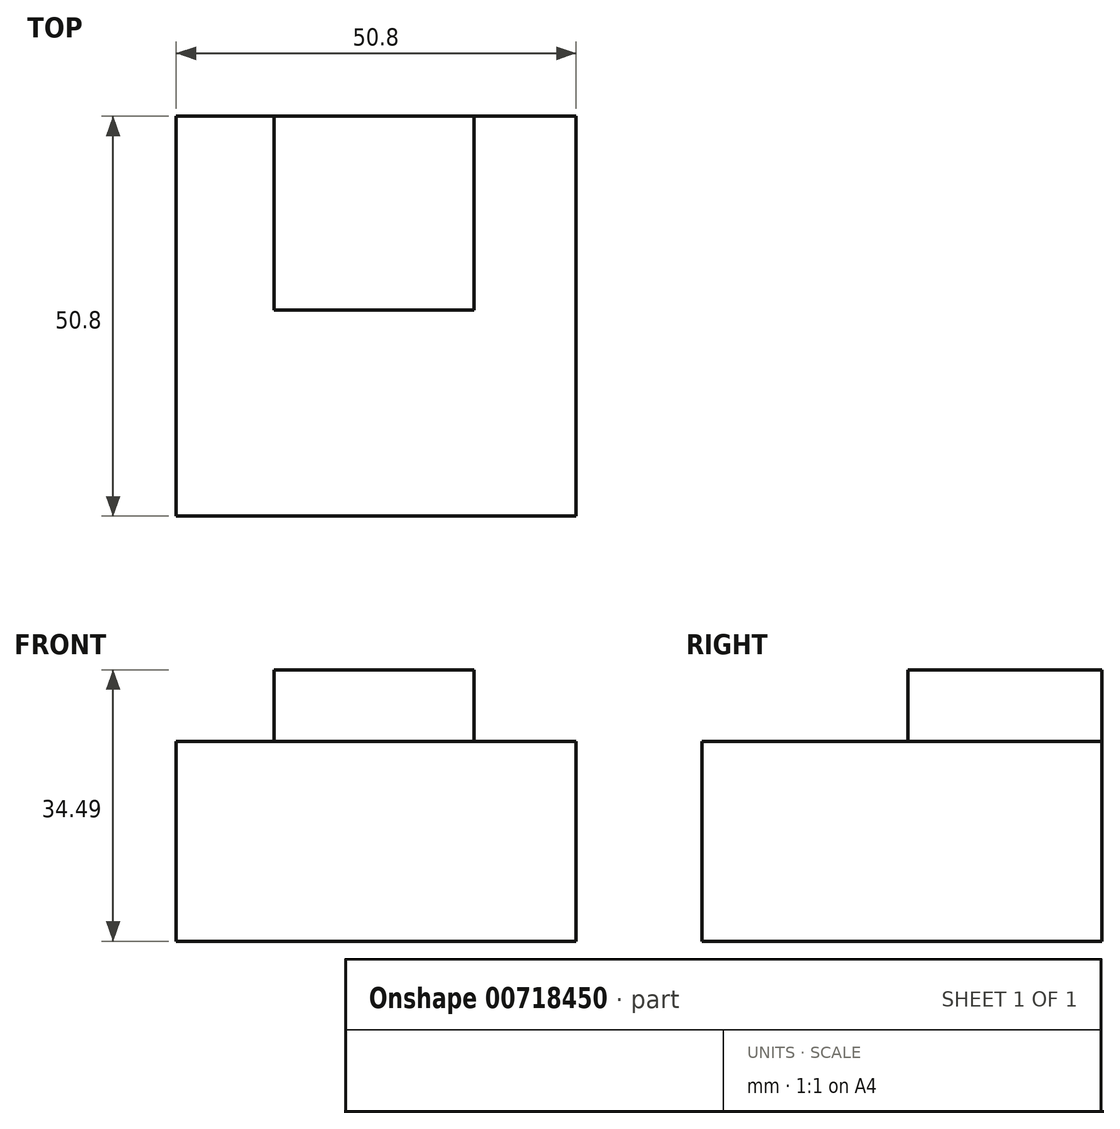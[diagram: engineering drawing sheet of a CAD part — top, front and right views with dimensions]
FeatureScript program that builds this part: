
annotation { "Feature Type Name" : "Feature", "Feature Type Description" : "" }
export const myFeature = defineFeature(function(context is Context, id is Id, definition is map)
    precondition{}
    {
        {
            var Q0;
            Q0=qCreatedBy(makeId("Front.planeOp"),FACE);
            var sketch = newSketch(context, id + "F0", { "sketchPlane" : qUnion([Q0])});
            skLineSegment(sketch, "E0", {"start": v(-56.1, 34.49) * mm, "end": v(-56.1, 9.09) * mm});
            skLineSegment(sketch, "E1", {"start": v(-56.1, 34.49) * mm, "end": v(-30.7, 34.49) * mm});
            skLineSegment(sketch, "E2", {"start": v(-30.7, 34.49) * mm, "end": v(-30.7, 9.09) * mm});
            skLineSegment(sketch, "E3", {"start": v(-30.7, 9.09) * mm, "end": v(-56.1, 9.09) * mm});
            skSolve(sketch);
        }
        {
            var Q0;
            Q0 = qSketchRegion(id + "F0", true);
            extrude(context, id + "F1", {"entities" : qUnion([Q0]), "depth" : 24.64 * mm, "offsetDistance" : 25.4 * mm});
        }
        {
            var Q0;
            Q0=qCreatedBy(makeId("Top.planeOp"),FACE);
            var sketch = newSketch(context, id + "F2", { "sketchPlane" : qUnion([Q0])});
            skLineSegment(sketch, "E4", {"start": v(-68.53, -50.8) * mm, "end": v(-68.53, 0) * mm});
            skLineSegment(sketch, "E5", {"start": v(-68.53, 0) * mm, "end": v(0, 0) * mm});
            skLineSegment(sketch, "E6", {"start": v(-68.53, 0) * mm, "end": v(-17.73, 0) * mm});
            skLineSegment(sketch, "E7", {"start": v(-17.73, 0) * mm, "end": v(-17.73, -50.8) * mm});
            skLineSegment(sketch, "E8", {"start": v(-17.73, -50.8) * mm, "end": v(-68.53, -50.8) * mm});
            skSolve(sketch);
        }
        {
            var Q0;
            Q0 = qSketchRegion(id + "F2", true);
            extrude(context, id + "F3", {"entities" : qUnion([Q0]), "operationType" : NewBodyOperationType.ADD, "depth" : 25.4 * mm, "offsetDistance" : 25.4 * mm});
        }
    });
